# Revit family: Sink-Vessel-Lavatory-KOHLER-Brazn-K-21060X
name_source: partatom
category: Plumbing Fixtures
units: mm (PartAtom-declared; Revit-internal decimal feet)

## family parameters
Cut with Voids When Loaded = No
Host = Face
OmniClass Number = 23.31.13.00
OmniClass Title = Sinks
Part Type = Normal
Room Calculation Point = No
Round Connector Dimension = Use Diameter
Shared = No

## types (5) — shared parameters
ADA Compliant = No
Assembly Code = D2010400
CW Connection = No
Cold Water Inlet = Cold Water Inlet
Date Modified = 12/19/2022
Default Elevation = 36"
Description = Rectangle Vessel Without Deck
Drain Included = Yes
Finish = Kohler-Vitreous_China-0-White
HW Connection = No
Height = 7"
Hot Water Inlet = Hot Water Inlet
Length = 23"
Manufacturer = Kohler Co.
Master Format 2014 = 22 41 16
Master Format 2014 Name = Residential Lavatories and Sinks
Material = Vitreous China
Product Name = Brazn
URL = https://www.kohlerasiapacific.com
Vent Connection = No
Waste Connection = Yes
Waste Water Outlet = Waste Water Outlet
WaterSense Certified = No
Width = 16"

## per-type parameters (varying)
| type | Model | Type |
| 0-White | K-21060X-0 | 1 |
| With Elle, 0-White | K-21060X-AE1-0 | 2 |
| With Nahu, 0-White | K-21060X-AE2-0 | 3 |
| With Kumari, 0-White | K-21060X-AE3-0 | 4 |
| With Ziling, 0-White | K-21060X-AE4-0 | 5 |

## geometry (parser evidence)
native form markers: Sweep x5
no freeform markers — native parametric forms only
